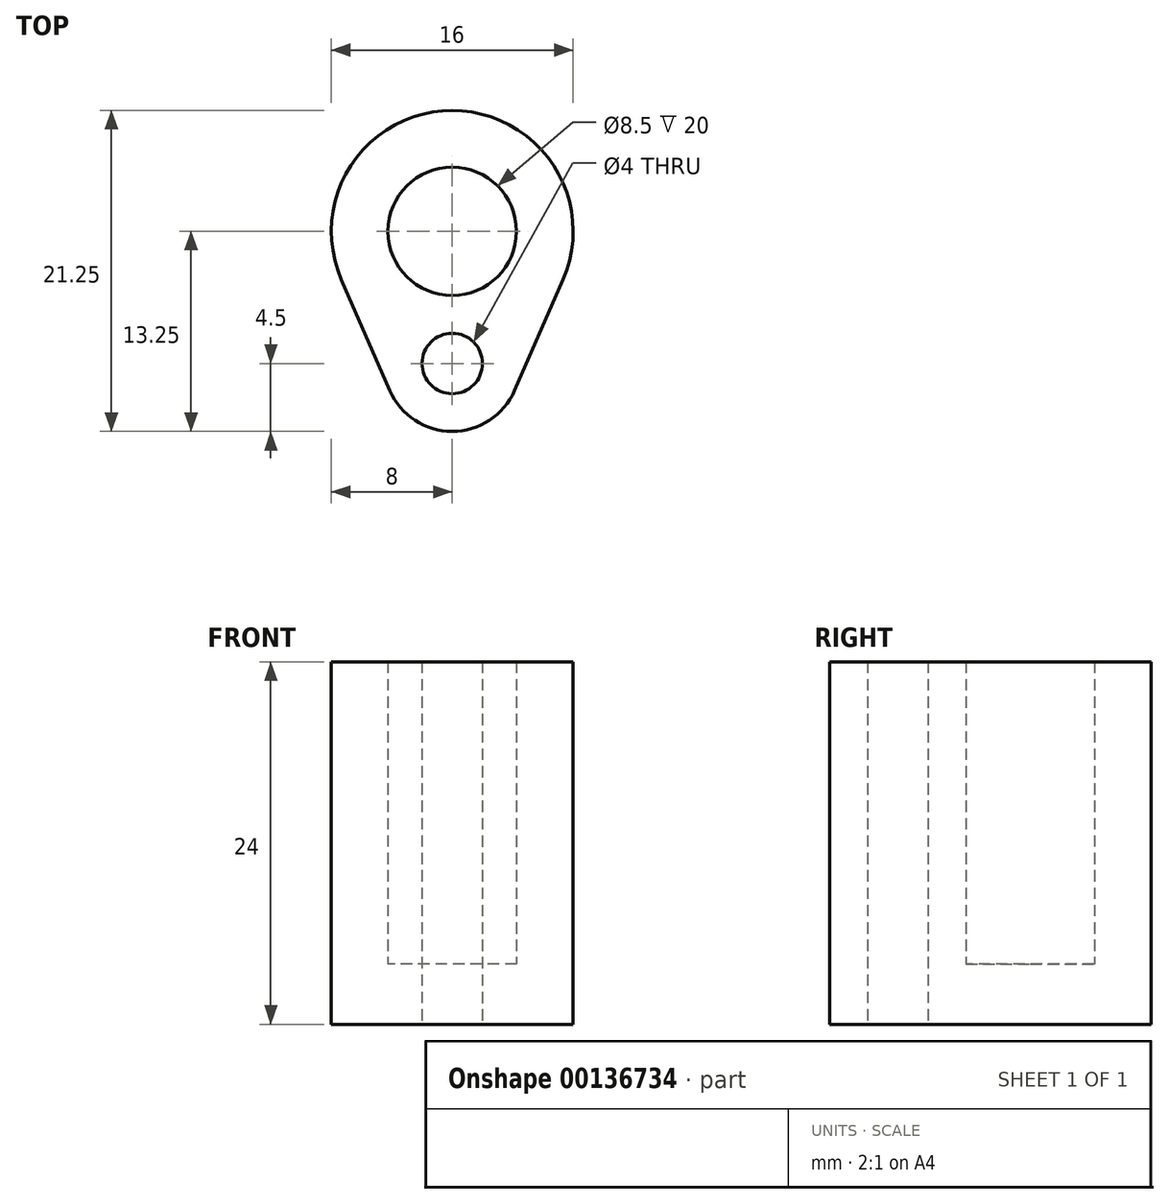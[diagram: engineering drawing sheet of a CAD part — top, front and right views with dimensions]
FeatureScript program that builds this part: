
annotation { "Feature Type Name" : "Feature", "Feature Type Description" : "" }
export const myFeature = defineFeature(function(context is Context, id is Id, definition is map)
    precondition{}
    {
        {
            var Q0;
            Q0=qCreatedBy(makeId("Top.planeOp"),FACE);
            var sketch = newSketch(context, id + "F0", { "sketchPlane" : qUnion([Q0])});
            skCircle(sketch, "E0", {"center": v(0, 0) * mm, "radius": 4.25 * mm});
            skArc(sketch, "E1", {"start": v(7.33, -3.2) * mm, "mid": v(0, 8) * mm, "end": v(-7.33, -3.2) * mm});
            skArc(sketch, "E2", {"start": v(-4.12, -10.55) * mm, "mid": v(0, -13.25) * mm, "end": v(4.12, -10.55) * mm});
            skCircle(sketch, "E3", {"center": v(0, -8.75) * mm, "radius": 2 * mm});
            skLineSegment(sketch, "E4", {"start": v(-4.12, -10.55) * mm, "end": v(-7.33, -3.2) * mm});
            skLineSegment(sketch, "E5", {"start": v(4.12, -10.55) * mm, "end": v(7.33, -3.2) * mm});
            skSolve(sketch);
        }
        {
            var Q0;
            Q0=makeQuery(id+"F0.imprint","IMPRINT",FACE,{"disambiguationData":[TD([[makeQuery(id+"F0.imprint","IMPRINT",EDGE,{"derivedFrom":sQuery(id+"F0.wireOp",EDGE,"E0")}),-1.0]])]});
            extrude(context, id + "F1", {"entities" : qUnion([Q0]), "depth" : 24 * mm});
        }
        {
            var Q0;
            Q0=makeQuery(id+"F0.imprint","IMPRINT",FACE,{"disambiguationData":[TD([[makeQuery(id+"F0.imprint","IMPRINT",EDGE,{"derivedFrom":sQuery(id+"F0.wireOp",EDGE,"E0")}),1.0]])]});
            extrude(context, id + "F2", {"entities" : qUnion([Q0]), "operationType" : NewBodyOperationType.ADD, "depth" : 4 * mm});
        }
    });
